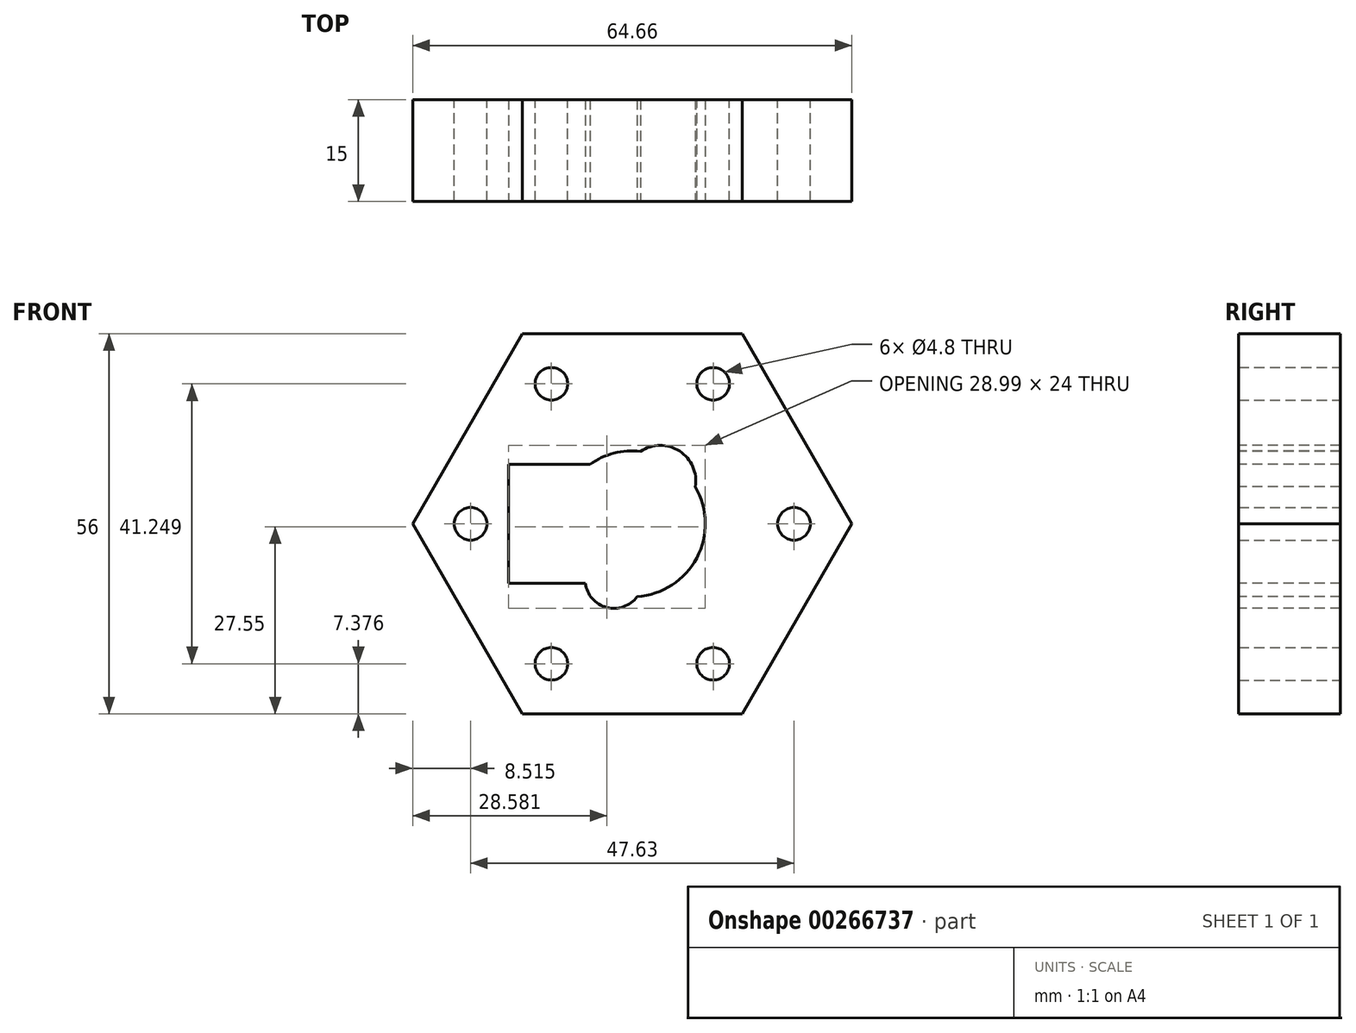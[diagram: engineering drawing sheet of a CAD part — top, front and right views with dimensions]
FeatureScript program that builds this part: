
annotation { "Feature Type Name" : "Feature", "Feature Type Description" : "" }
export const myFeature = defineFeature(function(context is Context, id is Id, definition is map)
    precondition{}
    {
        {
            var Q0;
            Q0=qCreatedBy(makeId("Front.planeOp"),FACE);
            var sketch = newSketch(context, id + "F0", { "sketchPlane" : qUnion([Q0])});
            skCircle(sketch, "E0.cCircle", {"center": v(0, 0) * mm, "radius": 28 * mm, "construction": true});
            skLineSegment(sketch, "E0.0", {"start": v(-16.17, 28) * mm, "end": v(16.17, 28) * mm});
            skLineSegment(sketch, "E0.1", {"start": v(16.17, 28) * mm, "end": v(32.33, 0) * mm});
            skLineSegment(sketch, "E0.2", {"start": v(32.33, 0) * mm, "end": v(16.17, -28) * mm});
            skLineSegment(sketch, "E0.3", {"start": v(16.17, -28) * mm, "end": v(-16.17, -28) * mm});
            skLineSegment(sketch, "E0.4", {"start": v(-16.17, -28) * mm, "end": v(-32.33, 0) * mm});
            skLineSegment(sketch, "E0.5", {"start": v(-32.33, 0) * mm, "end": v(-16.17, 28) * mm});
            skPoint(sketch, "E0.0.midPoint", {"position": v(0, 28) * mm});
            skCircle(sketch, "E1", {"center": v(0, 0) * mm, "radius": 23.82 * mm, "construction": true});
            skPoint(sketch, "E2", {"position": v(-23.82, 0) * mm});
            skPoint(sketch, "E3.1.0", {"position": v(-11.9, -20.62) * mm});
            skPoint(sketch, "E3.2.0", {"position": v(11.9, -20.62) * mm});
            skPoint(sketch, "E3.3.0", {"position": v(23.82, 0) * mm});
            skPoint(sketch, "E3.4.0", {"position": v(11.9, 20.62) * mm});
            skPoint(sketch, "E3.5.0", {"position": v(-11.9, 20.62) * mm});
            skCircle(sketch, "E4", {"center": v(11.9, 20.62) * mm, "radius": 2.4 * mm});
            skCircle(sketch, "E5.MirrorC", {"center": v(11.9, -20.62) * mm, "radius": 2.4 * mm});
            skCircle(sketch, "E6.MirrorC", {"center": v(-11.9, 20.62) * mm, "radius": 2.4 * mm});
            skCircle(sketch, "E7.MirrorC", {"center": v(-11.9, -20.62) * mm, "radius": 2.4 * mm});
            skCircle(sketch, "E8", {"center": v(-23.82, 0) * mm, "radius": 2.4 * mm});
            skCircle(sketch, "E9.MirrorC", {"center": v(23.82, 0) * mm, "radius": 2.4 * mm});
            skSolve(sketch);
        }
        {
            var Q0;
            Q0=makeQuery(id+"F0.imprint","IMPRINT",FACE,{"disambiguationData":[TD([[makeQuery(id+"F0.imprint","IMPRINT",EDGE,{"derivedFrom":sQuery(id+"F0.wireOp",EDGE,"E0.0")}),-1.0]])]});
            extrude(context, id + "F1", {"entities" : qUnion([Q0]), "offsetDistance" : 25 * mm, "depth" : 15 * mm});
        }
        {
            var Q0;
            Q0=makeQuery(id+"F1.opExtrude","CAP_FACE",FACE,{"disambiguationData":[OSD([sQuery(id+"F0.wireOp",EDGE,"E0.0"),sQuery(id+"F0.wireOp",EDGE,"E0.1"),sQuery(id+"F0.wireOp",EDGE,"E0.2"),sQuery(id+"F0.wireOp",EDGE,"E0.3"),sQuery(id+"F0.wireOp",EDGE,"E0.4"),sQuery(id+"F0.wireOp",EDGE,"E0.5"),sQuery(id+"F0.wireOp",EDGE,"E4"),sQuery(id+"F0.wireOp",EDGE,"E5.MirrorC"),sQuery(id+"F0.wireOp",EDGE,"E6.MirrorC"),sQuery(id+"F0.wireOp",EDGE,"E7.MirrorC"),sQuery(id+"F0.wireOp",EDGE,"E8"),sQuery(id+"F0.wireOp",EDGE,"E9.MirrorC")])],"isStart":false});
            var sketch = newSketch(context, id + "F2", { "sketchPlane" : qUnion([Q0])});
            skArc(sketch, "E10", {"start": v(0.72, -10.73) * mm, "mid": v(9.5, -5.03) * mm, "end": v(9.28, 5.43) * mm});
            skLineSegment(sketch, "E11.bottom", {"start": v(-6.91, -8.75) * mm, "end": v(-18.24, -8.75) * mm});
            skLineSegment(sketch, "E11.top", {"start": v(-6.24, 8.75) * mm, "end": v(-18.24, 8.75) * mm});
            skLineSegment(sketch, "E11.right", {"start": v(-18.24, -8.75) * mm, "end": v(-18.24, 8.75) * mm});
            skLineSegment(sketch, "E12", {"start": v(0, 0) * mm, "end": v(0, 6.3) * mm, "construction": true});
            skLineSegment(sketch, "E13", {"start": v(0, 6.3) * mm, "end": v(4.1, 6.3) * mm, "construction": true});
            skArc(sketch, "E14", {"start": v(9.28, 5.43) * mm, "mid": v(6.96, 10.7) * mm, "end": v(1.2, 10.68) * mm});
            skArc(sketch, "E15.MirrorC", {"start": v(-6.91, -8.75) * mm, "mid": v(-3.76, -12.32) * mm, "end": v(0.72, -10.73) * mm});
            skArc(sketch, "E16.trimOffspring", {"start": v(1.2, 10.68) * mm, "mid": v(-2.7, 10.4) * mm, "end": v(-6.24, 8.75) * mm});
            skSolve(sketch);
        }
        {
            var Q0;
            Q0=makeQuery(id+"F2.imprint","IMPRINT",FACE,{"disambiguationData":[TD([[makeQuery(id+"F2.imprint","IMPRINT",EDGE,{"derivedFrom":sQuery(id+"F2.wireOp",EDGE,"E10")}),1.0]])]});
            extrude(context, id + "F3", {"entities" : qUnion([Q0]), "operationType" : NewBodyOperationType.REMOVE, "oppositeDirection" : true, "depth" : 25 * mm});
        }
    });
